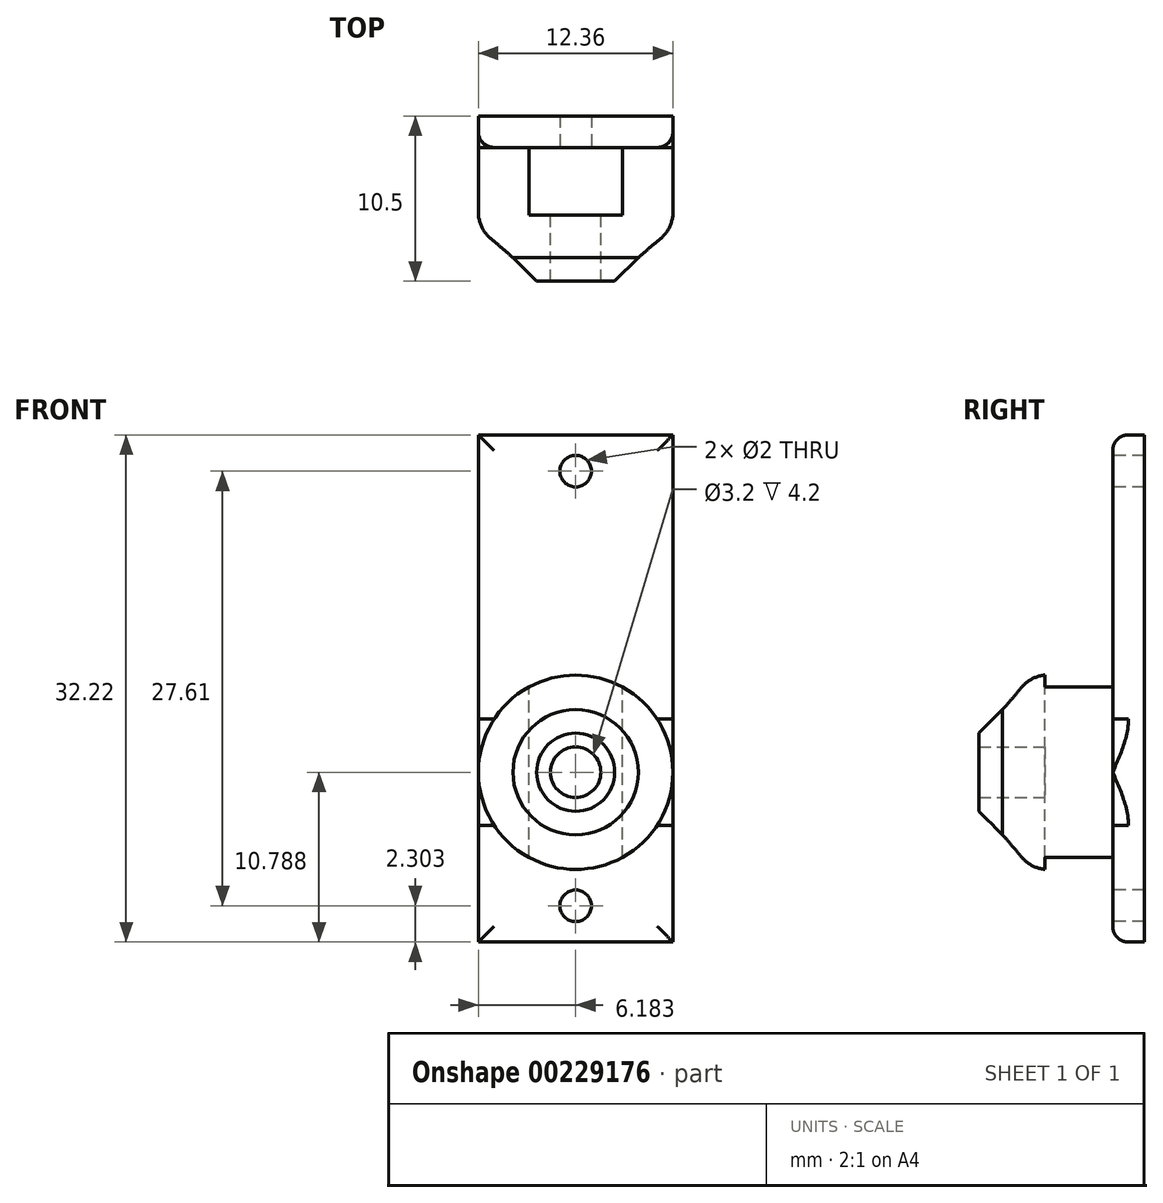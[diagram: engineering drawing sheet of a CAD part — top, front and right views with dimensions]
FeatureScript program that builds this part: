
annotation { "Feature Type Name" : "Feature", "Feature Type Description" : "" }
export const myFeature = defineFeature(function(context is Context, id is Id, definition is map)
    precondition{}
    {
        {
            var Q0;
            Q0=qCreatedBy(makeId("Front.planeOp"),FACE);
            var sketch = newSketch(context, id + "F0", { "sketchPlane" : qUnion([Q0])});
            skPoint(sketch, "E0.middle", {"position": v(0, 0) * mm});
            skLineSegment(sketch, "E1.left", {"start": v(10.15, -25.62) * mm, "end": v(10.15, 6.6) * mm});
            skLineSegment(sketch, "E1.right", {"start": v(-2.2, -25.62) * mm, "end": v(-2.2, 6.6) * mm});
            skLineSegment(sketch, "E2.left", {"start": v(-2.2, 6.6) * mm, "end": v(-2.2, -21.01) * mm});
            skLineSegment(sketch, "E2.right", {"start": v(10.15, 1.99) * mm, "end": v(10.15, -21.01) * mm});
            skCircle(sketch, "E3", {"center": v(3.97, 4.3) * mm, "radius": 1 * mm});
            skCircle(sketch, "E4", {"center": v(3.97, -14.83) * mm, "radius": 6.18 * mm});
            skCircle(sketch, "E5", {"center": v(3.97, -14.83) * mm, "radius": 1.6 * mm});
            skLineSegment(sketch, "E6.bottom", {"start": v(6.07, -16.88) * mm, "end": v(1.87, -16.88) * mm});
            skLineSegment(sketch, "E6.top", {"start": v(6.07, -12.78) * mm, "end": v(1.87, -12.78) * mm});
            skLineSegment(sketch, "E6.left", {"start": v(6.07, -16.88) * mm, "end": v(6.07, -12.78) * mm});
            skLineSegment(sketch, "E6.right", {"start": v(1.87, -16.88) * mm, "end": v(1.87, -12.78) * mm});
            skLineSegment(sketch, "E7.bottom", {"start": v(-2.2, -25.62) * mm, "end": v(10.15, -25.62) * mm});
            skLineSegment(sketch, "E7.top", {"start": v(-2.2, -21.01) * mm, "end": v(10.15, -21.01) * mm});
            skLineSegment(sketch, "E7.left", {"start": v(-2.2, -25.62) * mm, "end": v(-2.2, -21.01) * mm});
            skLineSegment(sketch, "E7.right", {"start": v(10.15, -25.62) * mm, "end": v(10.15, -21.01) * mm});
            skLineSegment(sketch, "E8.bottom", {"start": v(-2.2, 6.6) * mm, "end": v(10.15, 6.6) * mm});
            skLineSegment(sketch, "E8.top", {"start": v(-2.2, 1.99) * mm, "end": v(10.15, 1.99) * mm});
            skLineSegment(sketch, "E8.left", {"start": v(-2.2, 6.6) * mm, "end": v(-2.2, 1.99) * mm});
            skLineSegment(sketch, "E8.right", {"start": v(10.15, 6.6) * mm, "end": v(10.15, 1.99) * mm});
            skLineSegment(sketch, "E9", {"start": v(-2.2, -21.01) * mm, "end": v(10.15, -25.62) * mm, "construction": true});
            skLineSegment(sketch, "E10", {"start": v(-2.2, -25.62) * mm, "end": v(10.15, -21.01) * mm, "construction": true});
            skPoint(sketch, "E11", {"position": v(3.97, -23.32) * mm});
            skCircle(sketch, "E12", {"center": v(3.97, -23.32) * mm, "radius": 1 * mm});
            skLineSegment(sketch, "E13", {"start": v(-2.2, 6.6) * mm, "end": v(10.15, 1.99) * mm, "construction": true});
            skSolve(sketch);
        }
        {
            var Q0;
            {var subQ1=sQuery(id+"F0.wireOp",EDGE,"E1.right");var subQ3=sQuery(id+"F0.wireOp",EDGE,"E4");var subQ6=sQuery(id+"F0.wireOp",EDGE,"E7.bottom");var subQ7=sQuery(id+"F0.wireOp",EDGE,"E1.left");var subQ11=sQuery(id+"F0.wireOp",EDGE,"E8.top");var subQ14=makeQuery(id+"F0.imprint","IMPRINT",EDGE,{"derivedFrom":subQ11});var subQ15=makeQuery(id+"F0.imprint","INTERSECT",VERTEX,{"derivedFrom":[subQ7,subQ3]});var subQ17=makeQuery(id+"F0.imprint","INTERSECT",VERTEX,{"derivedFrom":[subQ1,subQ3]});Q0=qUnion([makeQuery(id+"F0.imprint","IMPRINT",FACE,{"disambiguationData":[TD([[makeQuery(id+"F0.imprint","IMPRINT",EDGE,{"derivedFrom":sQuery(id+"F0.wireOp",EDGE,"E6.bottom")}),1.0]])]}),makeQuery(id+"F0.imprint","IMPRINT",FACE,{"disambiguationData":[TD([[subQ14,-1.0]])]}),makeQuery(id+"F0.imprint","IMPRINT",FACE,{"disambiguationData":[TD([[makeQuery(id+"F0.imprint","IMPRINT",EDGE,{"disambiguationData":[TD([[subQ17,1.0]])],"derivedFrom":subQ1}),-1.0]])]}),makeQuery(id+"F0.imprint","IMPRINT",FACE,{"disambiguationData":[TD([[makeQuery(id+"F0.imprint","IMPRINT",EDGE,{"disambiguationData":[TD([[subQ15,1.0]])],"derivedFrom":subQ7}),1.0]])]}),makeQuery(id+"F0.imprint","IMPRINT",FACE,{"disambiguationData":[TD([[makeQuery(id+"F0.imprint","IMPRINT",EDGE,{"derivedFrom":sQuery(id+"F0.wireOp",EDGE,"E3")}),-1.0]])]}),makeQuery(id+"F0.imprint","IMPRINT",FACE,{"disambiguationData":[TD([[makeQuery(id+"F0.imprint","IMPRINT",EDGE,{"derivedFrom":subQ6}),1.0]])]})]);}
            var Q1;
            {var subQ4=sQuery(id+"F0.wireOp",EDGE,"cf8aaaef-a0c1-4cac-b1e5-4b45cacdd4bc.0");Q1=makeQuery(id+"F0.imprint","IMPRINT",FACE,{"disambiguationData":[TD([[makeQuery(id+"F0.imprint","IMPRINT",EDGE,{"derivedFrom":subQ4}),-1.0]])]});}
            var Q2;
            {var subQ0=sQuery(id+"F0.wireOp",EDGE,"cf8aaaef-a0c1-4cac-b1e5-4b45cacdd4bc.3");Q2=makeQuery(id+"F0.imprint","IMPRINT",FACE,{"disambiguationData":[TD([[makeQuery(id+"F0.imprint","IMPRINT",EDGE,{"derivedFrom":subQ0}),1.0]])]});}
            var Q3;
            {var subQ0=sQuery(id+"F0.wireOp",EDGE,"cf8aaaef-a0c1-4cac-b1e5-4b45cacdd4bc.4");Q3=makeQuery(id+"F0.imprint","IMPRINT",FACE,{"disambiguationData":[TD([[makeQuery(id+"F0.imprint","IMPRINT",EDGE,{"derivedFrom":subQ0}),1.0]])]});}
            var Q4;
            {var subQ0=sQuery(id+"F0.wireOp",EDGE,"cf8aaaef-a0c1-4cac-b1e5-4b45cacdd4bc.1");Q4=makeQuery(id+"F0.imprint","IMPRINT",FACE,{"disambiguationData":[TD([[makeQuery(id+"F0.imprint","IMPRINT",EDGE,{"derivedFrom":subQ0}),1.0]])]});}
            var Q5;
            {var subQ0=sQuery(id+"F0.wireOp",EDGE,"cf8aaaef-a0c1-4cac-b1e5-4b45cacdd4bc.0");Q5=makeQuery(id+"F0.imprint","IMPRINT",FACE,{"disambiguationData":[TD([[makeQuery(id+"F0.imprint","IMPRINT",EDGE,{"derivedFrom":subQ0}),1.0]])]});}
            var Q6;
            {var subQ3=sQuery(id+"F0.wireOp",EDGE,"E0.bottom");Q6=makeQuery(id+"F0.imprint","IMPRINT",FACE,{"disambiguationData":[TD([[makeQuery(id+"F0.imprint","IMPRINT",EDGE,{"derivedFrom":subQ3}),-1.0]])]});}
            var Q7;
            Q7=makeQuery(id+"F0.imprint","IMPRINT",FACE,{"disambiguationData":[TD([[makeQuery(id+"F0.imprint","IMPRINT",EDGE,{"derivedFrom":sQuery(id+"F0.wireOp",EDGE,"E5")}),1.0]])]});
            var Q8;
            Q8=makeQuery(id+"F0.imprint","IMPRINT",FACE,{"disambiguationData":[TD([[makeQuery(id+"F0.imprint","IMPRINT",EDGE,{"derivedFrom":sQuery(id+"F0.wireOp",EDGE,"E5")}),-1.0]])]});
            extrude(context, id + "F1", {"entities" : qUnion([Q0, Q1, Q2, Q3, Q4, Q5, Q6, Q7, Q8]), "oppositeDirection" : true, "depth" : 2 * mm});
        }
        {
            var Q0;
            {var subQ3=sQuery(id+"F0.wireOp",EDGE,"E0.bottom");Q0=makeQuery(id+"F0.imprint","IMPRINT",FACE,{"disambiguationData":[TD([[makeQuery(id+"F0.imprint","IMPRINT",EDGE,{"derivedFrom":subQ3}),1.0]])]});}
            var Q1;
            {var subQ3=sQuery(id+"F0.wireOp",EDGE,"E0.bottom");Q1=makeQuery(id+"F0.imprint","IMPRINT",FACE,{"disambiguationData":[TD([[makeQuery(id+"F0.imprint","IMPRINT",EDGE,{"derivedFrom":subQ3}),-1.0]])]});}
            var Q2;
            Q2=makeQuery(id+"F0.imprint","IMPRINT",FACE,{"disambiguationData":[TD([[makeQuery(id+"F0.imprint","IMPRINT",EDGE,{"derivedFrom":sQuery(id+"F0.wireOp",EDGE,"E6.bottom")}),1.0]])]});
            var Q3;
            Q3=makeQuery(id+"F0.imprint","IMPRINT",FACE,{"disambiguationData":[TD([[makeQuery(id+"F0.imprint","IMPRINT",EDGE,{"derivedFrom":sQuery(id+"F0.wireOp",EDGE,"E5")}),-1.0]])]});
            extrude(context, id + "F2", {"entities" : qUnion([Q0, Q1, Q2, Q3]), "operationType" : NewBodyOperationType.ADD, "depth" : 4.3 * mm + .9 * mm + 1.1 * mm});
        }
        {
            var Q0;
            {var subQ3=sQuery(id+"F0.wireOp",EDGE,"E0.bottom");Q0=makeQuery(id+"F0.imprint","IMPRINT",FACE,{"disambiguationData":[TD([[makeQuery(id+"F0.imprint","IMPRINT",EDGE,{"derivedFrom":subQ3}),-1.0]])]});}
            var Q1;
            Q1=makeQuery(id+"F0.imprint","IMPRINT",FACE,{"disambiguationData":[TD([[makeQuery(id+"F0.imprint","IMPRINT",EDGE,{"derivedFrom":sQuery(id+"F0.wireOp",EDGE,"E5")}),1.0]])]});
            extrude(context, id + "F3", {"entities" : qUnion([Q0, Q1]), "operationType" : NewBodyOperationType.REMOVE, "depth" : 4 * mm});
        }
        {
            var Q0;
            {var subQ0=sQuery(id+"F0.wireOp",EDGE,"E0.left");var subQ3=sQuery(id+"F0.wireOp",EDGE,"E4");Q0=makeQuery(id+"F9oB9o1exd6MhGU_1.boolean.opBoolean","SPLIT",EDGE,{"disambiguationData":[TD([makeQuery(id+"F3.boolean.opBoolean","COPY",FACE,{"derivedFrom":makeQuery(id+"F3.opExtrude","SWEPT_FACE",FACE,{"disambiguationData":[OSD([subQ0])]})})])],"derivedFrom":makeQuery(id+"F2.boolean.opBoolean","SPLIT",EDGE,{"disambiguationData":[OD(0.0)],"derivedFrom":makeQuery(id+"F2.opExtrude","CAP_EDGE",EDGE,{"disambiguationData":[OSD([subQ3])],"isStart":true})})});}
            var Q1;
            Q1=makeQuery(id+"F2.opExtrude","CAP_EDGE",EDGE,{"disambiguationData":[OSD([sQuery(id+"F0.wireOp",EDGE,"E4")])],"isStart":false});
            var Q2;
            {var subQ0=sQuery(id+"F0.wireOp",EDGE,"E0.right");var subQ3=sQuery(id+"F0.wireOp",EDGE,"E4");Q2=makeQuery(id+"F9oB9o1exd6MhGU_1.boolean.opBoolean","SPLIT",EDGE,{"disambiguationData":[TD([makeQuery(id+"F3.boolean.opBoolean","COPY",FACE,{"derivedFrom":makeQuery(id+"F3.opExtrude","SWEPT_FACE",FACE,{"disambiguationData":[OSD([subQ0])]})})])],"derivedFrom":makeQuery(id+"F2.boolean.opBoolean","SPLIT",EDGE,{"disambiguationData":[OD(0.0)],"derivedFrom":makeQuery(id+"F2.opExtrude","CAP_EDGE",EDGE,{"disambiguationData":[OSD([subQ3])],"isStart":true})})});}
            fillet(context, id + "F4", {"entities" : qUnion([Q0, Q1, Q2]), "radius" : 2.2 * mm, "tangentPropagation" : true, "allowEdgeOverflow" : false});
        }
        {
            var Q0;
            Q0=qCreatedBy(makeId("Top.planeOp"),FACE);
            var sketch = newSketch(context, id + "F5", { "sketchPlane" : qUnion([Q0])});
            skLineSegment(sketch, "E14.bottom", {"start": v(6.95, 0) * mm, "end": v(1, 0) * mm});
            skLineSegment(sketch, "E14.top", {"start": v(6.95, -4.3) * mm, "end": v(1, -4.3) * mm});
            skLineSegment(sketch, "E14.left", {"start": v(6.95, 0) * mm, "end": v(6.95, -4.3) * mm});
            skLineSegment(sketch, "E14.right", {"start": v(1, 0) * mm, "end": v(1, -4.3) * mm});
            skSolve(sketch);
        }
        {
            var Q0;
            Q0 = qSketchRegion(id + "F5", true);
            extrude(context, id + "F6", {"entities" : qUnion([Q0]), "operationType" : NewBodyOperationType.REMOVE, "oppositeDirection" : true, "depth" : 25 * mm});
        }
        {
            var Q0;
            {var subQ0=sQuery(id+"F0.wireOp",EDGE,"E1.left");var subQ1=sQuery(id+"F0.wireOp",EDGE,"E8.bottom");Q0=makeQuery(id+"F2.boolean.opBoolean","SPLIT",EDGE,{"disambiguationData":[TD([makeQuery(id+"F1.opExtrude","SWEPT_FACE",FACE,{"disambiguationData":[OSD([subQ1])]})])],"derivedFrom":makeQuery(id+"F1.opExtrude","CAP_EDGE",EDGE,{"disambiguationData":[OSD([subQ0])],"isStart":true})});}
            var Q1;
            {var subQ0=sQuery(id+"F0.wireOp",EDGE,"E8.bottom");var subQ1=sQuery(id+"F0.wireOp",EDGE,"E1.right");Q1=makeQuery(id+"F2.boolean.opBoolean","SPLIT",EDGE,{"disambiguationData":[TD([makeQuery(id+"F1.opExtrude","SWEPT_FACE",FACE,{"disambiguationData":[OSD([subQ0])]})])],"derivedFrom":makeQuery(id+"F1.opExtrude","CAP_EDGE",EDGE,{"disambiguationData":[OSD([subQ1])],"isStart":true})});}
            var Q2;
            {var subQ0=sQuery(id+"F0.wireOp",EDGE,"E7.bottom");var subQ1=sQuery(id+"F0.wireOp",EDGE,"E1.right");Q2=makeQuery(id+"F2.boolean.opBoolean","SPLIT",EDGE,{"disambiguationData":[TD([makeQuery(id+"F1.opExtrude","SWEPT_FACE",FACE,{"disambiguationData":[OSD([subQ0])]})])],"derivedFrom":makeQuery(id+"F1.opExtrude","CAP_EDGE",EDGE,{"disambiguationData":[OSD([subQ1])],"isStart":true})});}
            var Q3;
            {var subQ0=sQuery(id+"F0.wireOp",EDGE,"E1.left");var subQ1=sQuery(id+"F0.wireOp",EDGE,"E7.bottom");Q3=makeQuery(id+"F2.boolean.opBoolean","SPLIT",EDGE,{"disambiguationData":[TD([makeQuery(id+"F1.opExtrude","SWEPT_FACE",FACE,{"disambiguationData":[OSD([subQ1])]})])],"derivedFrom":makeQuery(id+"F1.opExtrude","CAP_EDGE",EDGE,{"disambiguationData":[OSD([subQ0])],"isStart":true})});}
            var Q4;
            Q4=makeQuery(id+"F1.opExtrude","CAP_EDGE",EDGE,{"disambiguationData":[OSD([sQuery(id+"F0.wireOp",EDGE,"E7.bottom")])],"isStart":true});
            var Q5;
            Q5=makeQuery(id+"F1.opExtrude","CAP_EDGE",EDGE,{"disambiguationData":[OSD([sQuery(id+"F0.wireOp",EDGE,"E8.bottom")])],"isStart":true});
            fillet(context, id + "F7", {"entities" : qUnion([Q0, Q1, Q2, Q3, Q4, Q5]), "radius" : 1 * mm, "tangentPropagation" : true, "allowEdgeOverflow" : false});
        }
        {
            var Q0;
            Q0=makeQuery(id+"F2.opExtrude","CAP_FACE",FACE,{"disambiguationData":[OSD([sQuery(id+"F0.wireOp",EDGE,"E4"),sQuery(id+"F0.wireOp",EDGE,"E5")])],"isStart":false});
            var sketch = newSketch(context, id + "F8", { "sketchPlane" : qUnion([Q0])});
            skCircle(sketch, "E15", {"center": v(3.97, -14.83) * mm, "radius": 3.98 * mm});
            skCircle(sketch, "E16", {"center": v(3.97, -14.83) * mm, "radius": 1.6 * mm});
            skSolve(sketch);
        }
        {
            var Q0;
            Q0 = qSketchRegion(id + "F8", true);
            extrude(context, id + "F9", {"entities" : qUnion([Q0]), "operationType" : NewBodyOperationType.ADD, "depth" : 2.2 * mm});
        }
        {
            var Q0;
            Q0=makeQuery(id+"F9.opExtrude","CAP_EDGE",EDGE,{"disambiguationData":[OSD([sQuery(id+"F8.wireOp",EDGE,"E15")])],"isStart":false});
            chamfer(context, id + "F10", {"entities" : qUnion([Q0]), "width" : 1.5 * mm, "tangentPropagation" : true});
        }
        {
            var Q0;
            {var subQ0=sQuery(id+"F0.wireOp",EDGE,"E4");Q0=makeQuery(id+"F9.boolean.opBoolean","MERGE",EDGE,{"derivedFrom":[makeQuery(id+"F4.opFillet","BLEND_EDGE",EDGE,{"blendedFrom":[makeQuery(id+"F2.opExtrude","CAP_EDGE",EDGE,{"disambiguationData":[OSD([subQ0])],"isStart":false}),makeQuery(id+"F2.opExtrude","CAP_FACE",FACE,{"disambiguationData":[OSD([subQ0,sQuery(id+"F0.wireOp",EDGE,"E5")])],"isStart":false})],"blendedInto":[makeQuery(id+"F2.opExtrude","CAP_FACE",FACE,{"disambiguationData":[OSD([subQ0,sQuery(id+"F0.wireOp",EDGE,"E5")])],"isStart":false})]}),makeQuery(id+"F9.opExtrude","CAP_EDGE",EDGE,{"disambiguationData":[OSD([sQuery(id+"F8.wireOp",EDGE,"E15")])],"isStart":true})]});}
            fillet(context, id + "F11", {"entities" : qUnion([Q0]), "radius" : 40 * mm, "tangentPropagation" : true, "allowEdgeOverflow" : false});
        }
    });
